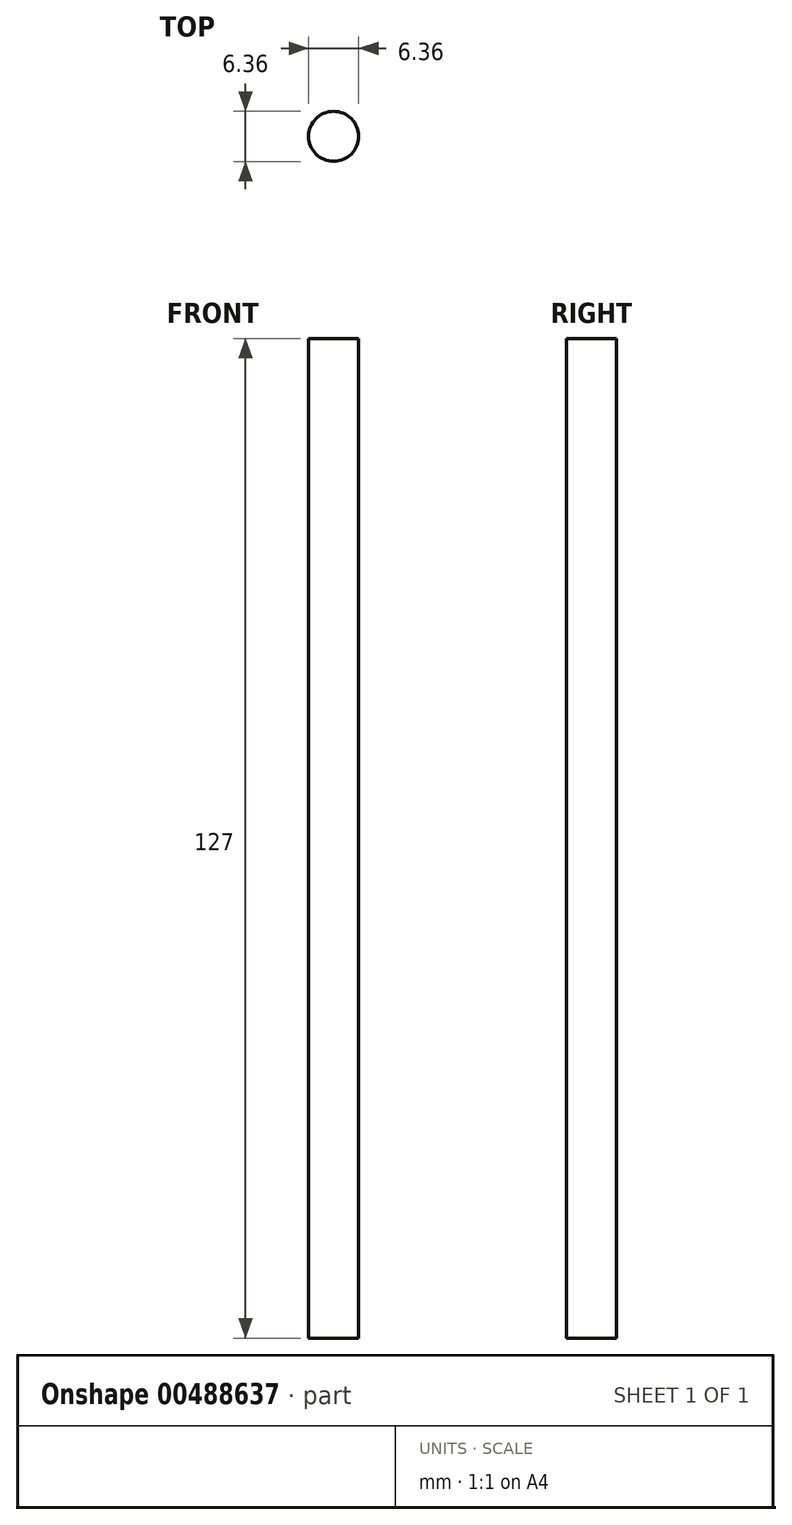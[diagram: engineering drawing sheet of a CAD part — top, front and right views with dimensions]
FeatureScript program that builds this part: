
annotation { "Feature Type Name" : "Feature", "Feature Type Description" : "" }
export const myFeature = defineFeature(function(context is Context, id is Id, definition is map)
    precondition{}
    {
        {
            var Q0;
            Q0=qCreatedBy(makeId("Top.planeOp"),FACE);
            var sketch = newSketch(context, id + "F0", { "sketchPlane" : qUnion([Q0])});
            skCircle(sketch, "E0", {"center": v(0, 0) * mm, "radius": 3.18 * mm});
            skSolve(sketch);
        }
        {
            var Q0;
            Q0=makeQuery(id+"F0.imprint","IMPRINT",FACE,{"disambiguationData":[TD([[makeQuery(id+"F0.imprint","IMPRINT",EDGE,{"derivedFrom":sQuery(id+"F0.wireOp",EDGE,"E0")}),1.0]])]});
            extrude(context, id + "F1", {"entities" : qUnion([Q0]), "depth" : 127 * mm});
        }
    });
